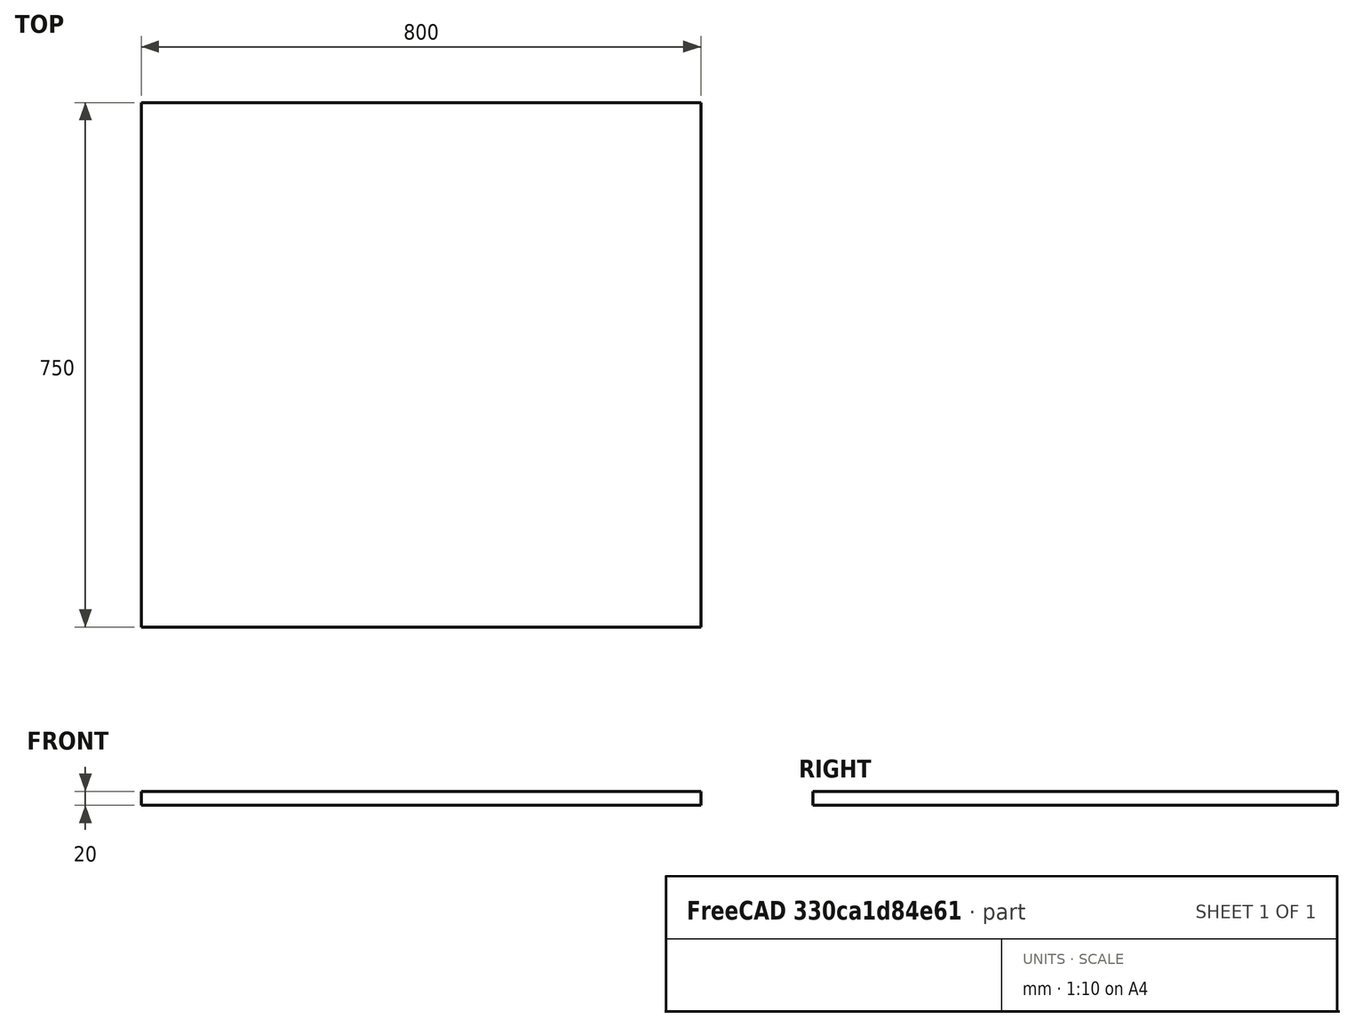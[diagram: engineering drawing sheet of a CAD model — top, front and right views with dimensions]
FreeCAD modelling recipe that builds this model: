
FCSTD DOCUMENT  (FreeCAD 0.20R29603 (Git))
Label: PlatteOben
License: All rights reserved
LicenseURL: http://en.wikipedia.org/wiki/All_rights_reserved
objects: Sketcher::SketchObject×1, PartDesign::Pad×1, PartDesign::Body×1
note: 4 computed .brp shape members not serialized (recipe doc carries the construction recipe); baked Part::Feature solids carry a one-line shape summary decoded from their .brp

FEATURE [Sketcher::SketchObject] Sketch
  FullyConstrained = true
  MapMode = 5
  Support = -> [XY_Plane]
  sketch-geometry (5):
    g0: LineSegment StartX=-400 StartY=375 StartZ=0 EndX=-400 EndY=-375 EndZ=0
    g1: LineSegment StartX=-400 StartY=-375 StartZ=0 EndX=400 EndY=-375 EndZ=0
    g2: LineSegment StartX=400 StartY=-375 StartZ=0 EndX=400 EndY=375 EndZ=0
    g3: LineSegment StartX=400 StartY=375 StartZ=0 EndX=-400 EndY=375 EndZ=0
    g4: GeomPoint X=0 Y=0 Z=0
  constraints (12):
    c: Coincident(g0,g1)
    c: Coincident(g1,g2)
    c: Coincident(g2,g3)
    c: Coincident(g3,g0)
    c: Horizontal(g1)
    c: Horizontal(g3)
    c: Vertical(g0)
    c: Vertical(g2)
    c: Symmetric(g1,g0,g4)
    c: Coincident(g4,g-1)
    c: Distance(g3) = 800
    c: Distance(g0) = 750
FEATURE [PartDesign::Pad] Pad
  Direction = (0,0,1)
  Length = 20
  Length2 = 10
  Profile = -> Sketch
  ReferenceAxis = -> Sketch [N_Axis]
  Type = 0
FEATURE [PartDesign::Body] Body
  Group = -> [Sketch,Pad]
  Origin = -> Origin
  Tip = -> Pad
